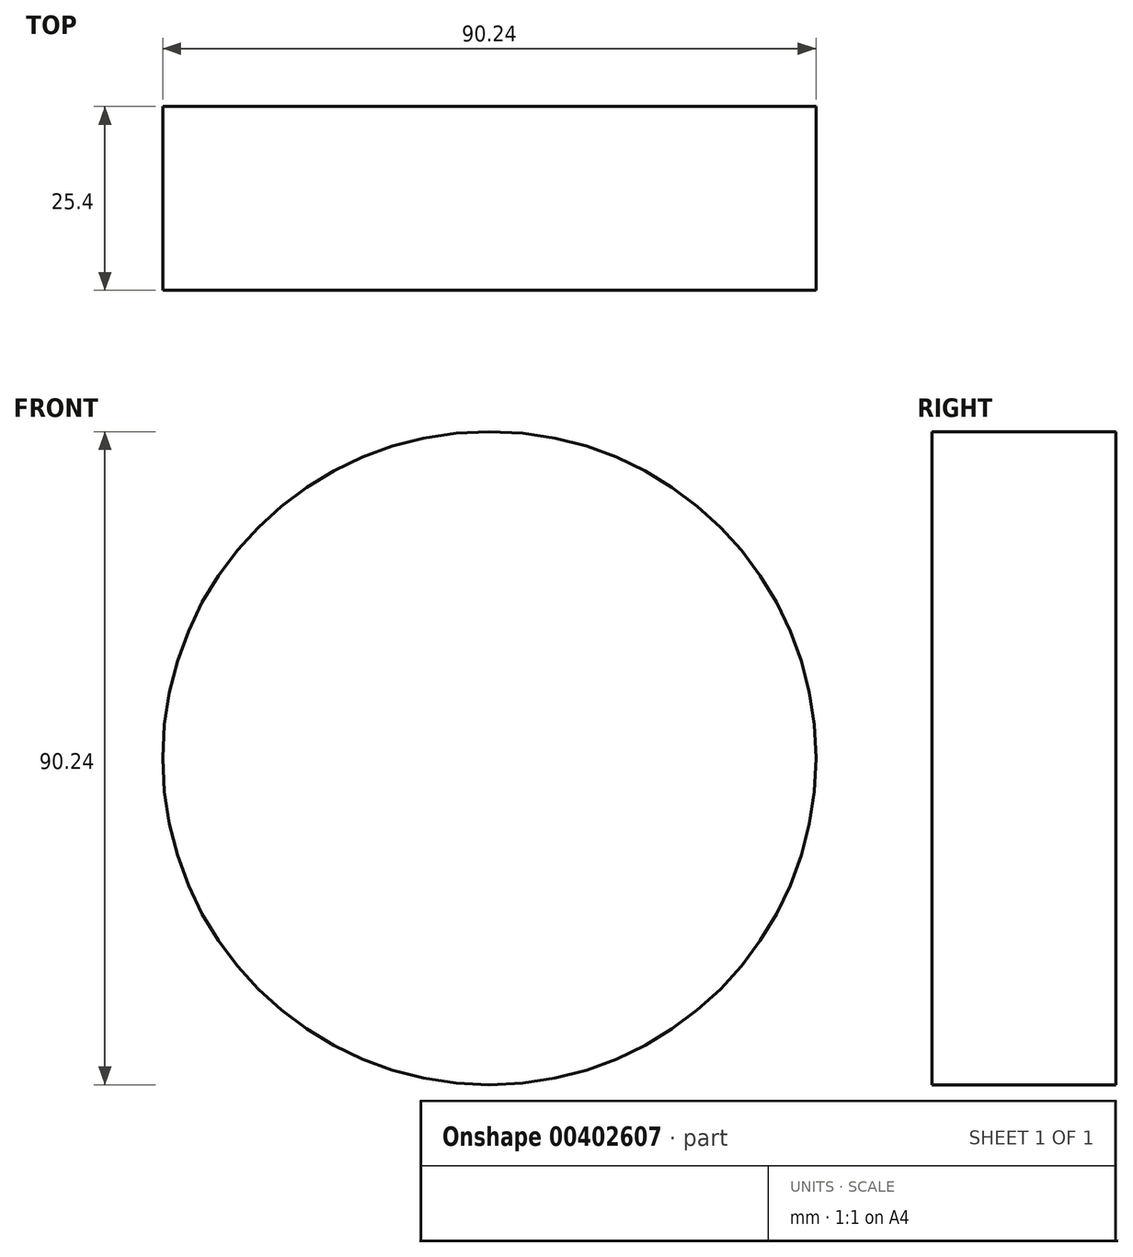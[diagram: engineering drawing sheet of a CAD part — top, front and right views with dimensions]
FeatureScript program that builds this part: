
annotation { "Feature Type Name" : "Feature", "Feature Type Description" : "" }
export const myFeature = defineFeature(function(context is Context, id is Id, definition is map)
    precondition{}
    {
        {
            var Q0;
            Q0=qCreatedBy(makeId("Front.planeOp"),FACE);
            var sketch = newSketch(context, id + "F0", { "sketchPlane" : qUnion([Q0])});
            skCircle(sketch, "E0", {"center": v(-38.5, 32.4) * mm, "radius": 45.12 * mm});
            skSolve(sketch);
        }
        {
            var Q0;
            Q0=makeQuery(id+"F0.imprint","IMPRINT",FACE,{"disambiguationData":[TD([[makeQuery(id+"F0.imprint","IMPRINT",EDGE,{"derivedFrom":sQuery(id+"F0.wireOp",EDGE,"E0")}),1.0]])]});
            extrude(context, id + "F1", {"entities" : qUnion([Q0]), "depth" : 25.4 * mm});
        }
    });
